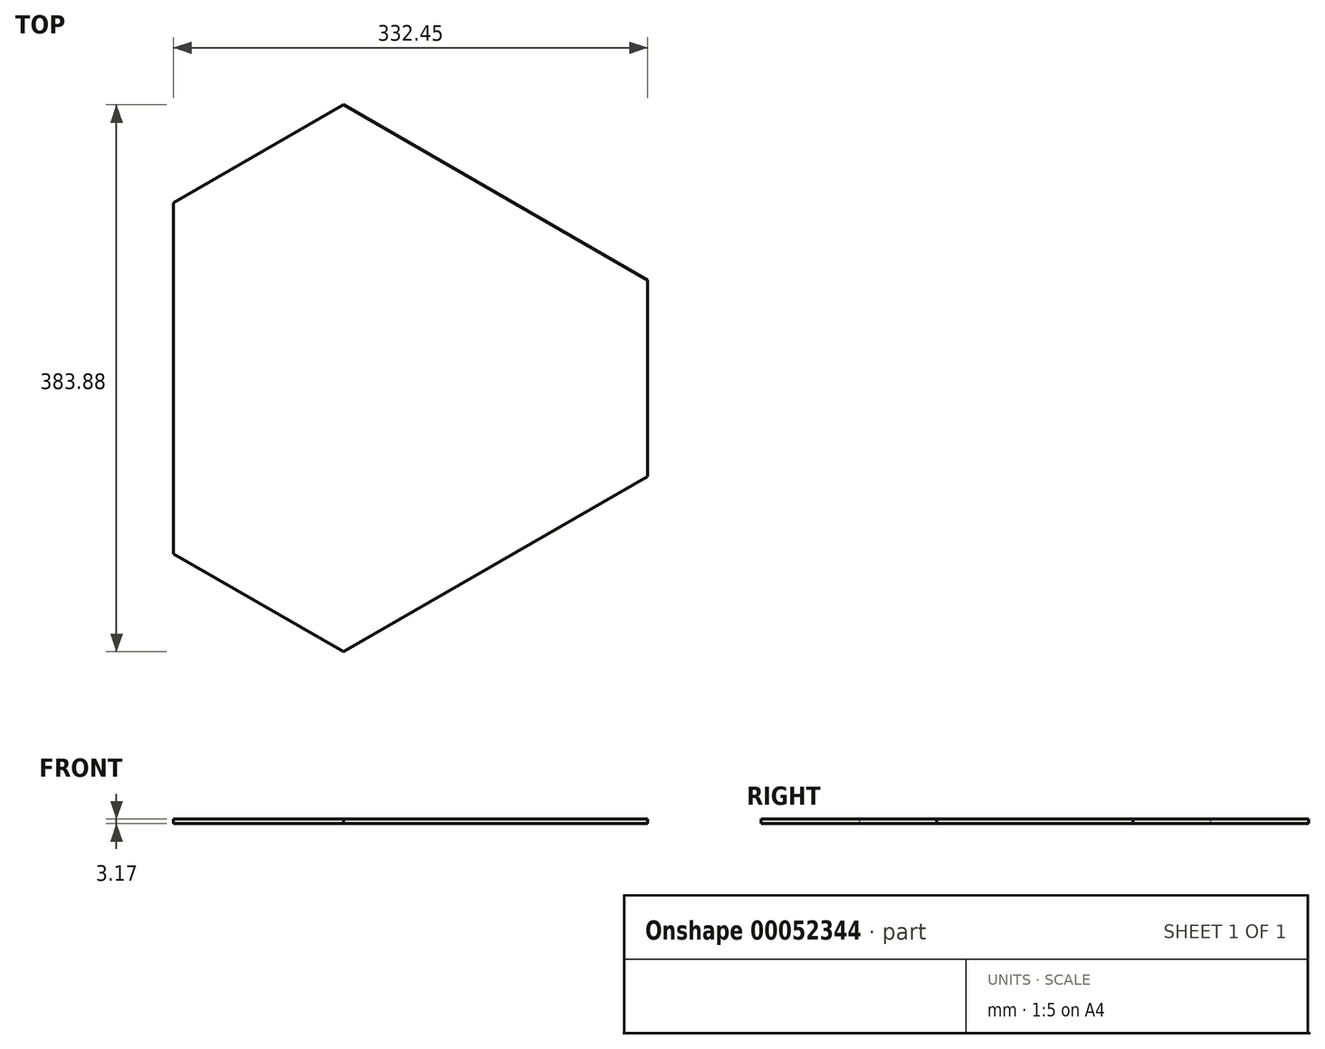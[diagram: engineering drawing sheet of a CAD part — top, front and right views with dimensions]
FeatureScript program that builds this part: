
annotation { "Feature Type Name" : "Feature", "Feature Type Description" : "" }
export const myFeature = defineFeature(function(context is Context, id is Id, definition is map)
    precondition{}
    {
        {
            var Q0;
            Q0=qCreatedBy(makeId("Top.planeOp"),FACE);
            var sketch = newSketch(context, id + "F0", { "sketchPlane" : qUnion([Q0])});
            skCircle(sketch, "E0.cCircle", {"center": v(0, 0) * mm, "radius": 175.98 * mm, "construction": true});
            skLineSegment(sketch, "E0.0", {"start": v(-175.98, -304.8) * mm, "end": v(-175.98, 304.8) * mm});
            skLineSegment(sketch, "E0.1", {"start": v(-175.98, 304.8) * mm, "end": v(351.95, 0) * mm});
            skLineSegment(sketch, "E0.2", {"start": v(351.95, 0) * mm, "end": v(-175.98, -304.8) * mm});
            skPoint(sketch, "E0.0.midPoint", {"position": v(-175.98, 0) * mm});
            skLineSegment(sketch, "E1.0", {"start": v(301.15, 0) * mm, "end": v(-150.58, -260.8) * mm});
            skLineSegment(sketch, "E1.1", {"start": v(-150.58, 260.8) * mm, "end": v(301.15, 0) * mm});
            skLineSegment(sketch, "E1.2", {"start": v(-150.58, -260.8) * mm, "end": v(-150.58, 260.8) * mm});
            skLineSegment(sketch, "E2", {"start": v(-18.6, 184.6) * mm, "end": v(-150.58, 108.4) * mm});
            skLineSegment(sketch, "E3.1.0", {"start": v(169.17, -76.2) * mm, "end": v(169.17, 76.2) * mm});
            skLineSegment(sketch, "E3.2.0", {"start": v(-150.58, -108.4) * mm, "end": v(-18.6, -184.6) * mm});
            skLineSegment(sketch, "E3.anchor1", {"start": v(0, 0) * mm, "end": v(-18.6, 184.6) * mm, "construction": true});
            skLineSegment(sketch, "E3.anchor2", {"start": v(0, 0) * mm, "end": v(-150.58, -108.4) * mm, "construction": true});
            skLineSegment(sketch, "E4.0", {"start": v(-24.94, 195.6) * mm, "end": v(-156.93, 119.4) * mm});
            skLineSegment(sketch, "E5.0", {"start": v(-156.93, -119.4) * mm, "end": v(-24.94, -195.6) * mm});
            skLineSegment(sketch, "E6.0", {"start": v(181.87, -76.2) * mm, "end": v(181.87, 76.2) * mm});
            skSolve(sketch);
        }
        {
            var Q0;
            {var subQ0=sQuery(id+"F0.wireOp",EDGE,"E2");Q0=makeQuery(id+"F0.imprint","IMPRINT",FACE,{"disambiguationData":[TD([[makeQuery(id+"F0.imprint","IMPRINT",EDGE,{"derivedFrom":subQ0}),1.0]])]});}
            var Q1;
            {var subQ0=sQuery(id+"F0.wireOp",EDGE,"E3.2.0");Q1=makeQuery(id+"F0.imprint","IMPRINT",FACE,{"disambiguationData":[TD([[makeQuery(id+"F0.imprint","IMPRINT",EDGE,{"derivedFrom":subQ0}),-1.0]])]});}
            var Q2;
            {var subQ0=sQuery(id+"F0.wireOp",EDGE,"E2");Q2=makeQuery(id+"F0.imprint","IMPRINT",FACE,{"disambiguationData":[TD([[makeQuery(id+"F0.imprint","IMPRINT",EDGE,{"derivedFrom":subQ0}),-1.0]])]});}
            var Q3;
            {var subQ0=sQuery(id+"F0.wireOp",EDGE,"E3.1.0");Q3=makeQuery(id+"F0.imprint","IMPRINT",FACE,{"disambiguationData":[TD([[makeQuery(id+"F0.imprint","IMPRINT",EDGE,{"derivedFrom":subQ0}),-1.0]])]});}
            extrude(context, id + "F1", {"entities" : qUnion([Q0, Q1, Q2, Q3]), "depth" : 3.17 * mm});
        }
    });
